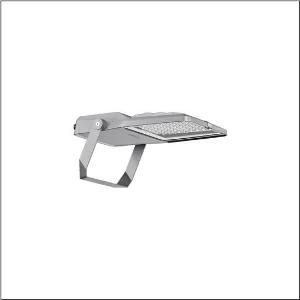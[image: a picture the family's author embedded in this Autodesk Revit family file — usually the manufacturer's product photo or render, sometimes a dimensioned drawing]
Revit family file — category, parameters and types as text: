
# Revit family: floodlight_fl_21_iq_mini___pl33t_5xa7771d2f1a_9c88
name_source: partatom
category: Lighting Fixtures
units: mm (PartAtom-declared; Revit-internal decimal feet)

## family parameters
Cut with Voids When Loaded = No
Host = Face
Light Source = No
Part Type = Normal
Room Calculation Point = No
Round Connector Dimension = Use Diameter
Shared = No

## types (1)
- --- (1 x LED, 17620 lm, 143 W, 3000K)
    Apparent Load = 143 VA
    CIE Flux Codes = 26 75 99 100 100
    Color Rendering = 70
    Color Temperature = 3000K
    Default Elevation = 1800 mm
    Description = Floodlight FL 21 iQ mini, floodlight, primary light control with lens, of PMMA, primary optical cover: protective disc, of toughened safety glass, transparent, light distribution: PL33T, light emission: direct distribution, installation type: surface-mounted, LED, High Power LED, rated luminous flux: 17.620lm, luminous efficacy: 123lm/W, light colour: 730, colour temperature: 3000K, control: Auto-Match, Temp-Guard, Lumen-Switch, Night-Set, Smart-Wire, Light-Fading, Desk-Remote (wireless, voltage-free reading and setting of iQ features in the workshop via application-optimized NFC function/RFID function), optimised constant luminous flux control (CLO 2.0), with terminal, 6-pole, mains connection: 220..240V, AC, 50/60Hz, start of lifetime: 143W, end of service life: 152W, reduction: 61W, luminaire housing, of diecast aluminium, powder-coated, Siteco® metallic grey (DB 702S), corrosivity category C5 mid according to DIN EN ISO 12944, sealing non-destructively replaceable, mounting bracket, of steel, galvanised, powder-coated, Siteco® metallic grey (DB 702S), protection rating (complete): IP66, insulation class (complete): insulation class II (safety insulation), certification: CE, ENEC, VDE, protection symbol: D, impact resistance: IK08, permissible operating ambient temperature: -40..+40°C, permissible operating ambient temperature for outdoor applications: -40..+50°C, standard: DIN EN 12944, LABS conformity tested according to VDMA 24364:2018-05, packaging unit: 1 piece

Light Distribution: PL33T
    Height = 70 mm
    Lamp = 1 x LED
    Lamp Light Flux = 17620 lm
    Lamp Power = 143 W
    Lamp count = 1
    Length = 485 mm
    Luminous efficacy = 123 lm/W
    Manufacturer = Siteco
    ModVariant = No
    Model = 5XA7771D2F1A
    Number of Poles = 1
    OnlyDefault = Yes
    Power Factor = 1
    Product Name = Floodlight FL 21 iQ mini | PL33T
    Product group = floodlight | pylon annexe
    ProductGroupID = 6200
    Protection Class = Protection class II
    Protection Degree = IP 66
    RLX_Detail_Level = 1
    RLX_Emergency_Light_Flux = 0 lm
    RLX_Emergency_Type = 0
    RLX_Emergency_Type_DB = No
    RlxData = <blob elided: 96225 chars, md5=b4f37115>
    Socket = socket
    Standby Power = 0 W
    System Light Flux = 17620 lm
    System Power = 143 W
    Type Comments = factory setting: luminous flux: 100 % | dim-lin: 254 | 730 mA
    Type Image = l_1006845.jpg
    URL = http://relux.com
    VarID = @adj_081757
    Voltage = 0 V
    Weight = 0.00 kg
    Width = 337 mm

## geometry (parser evidence)
native form markers: Blend x4, Sweep x10
no freeform markers — native parametric forms only
